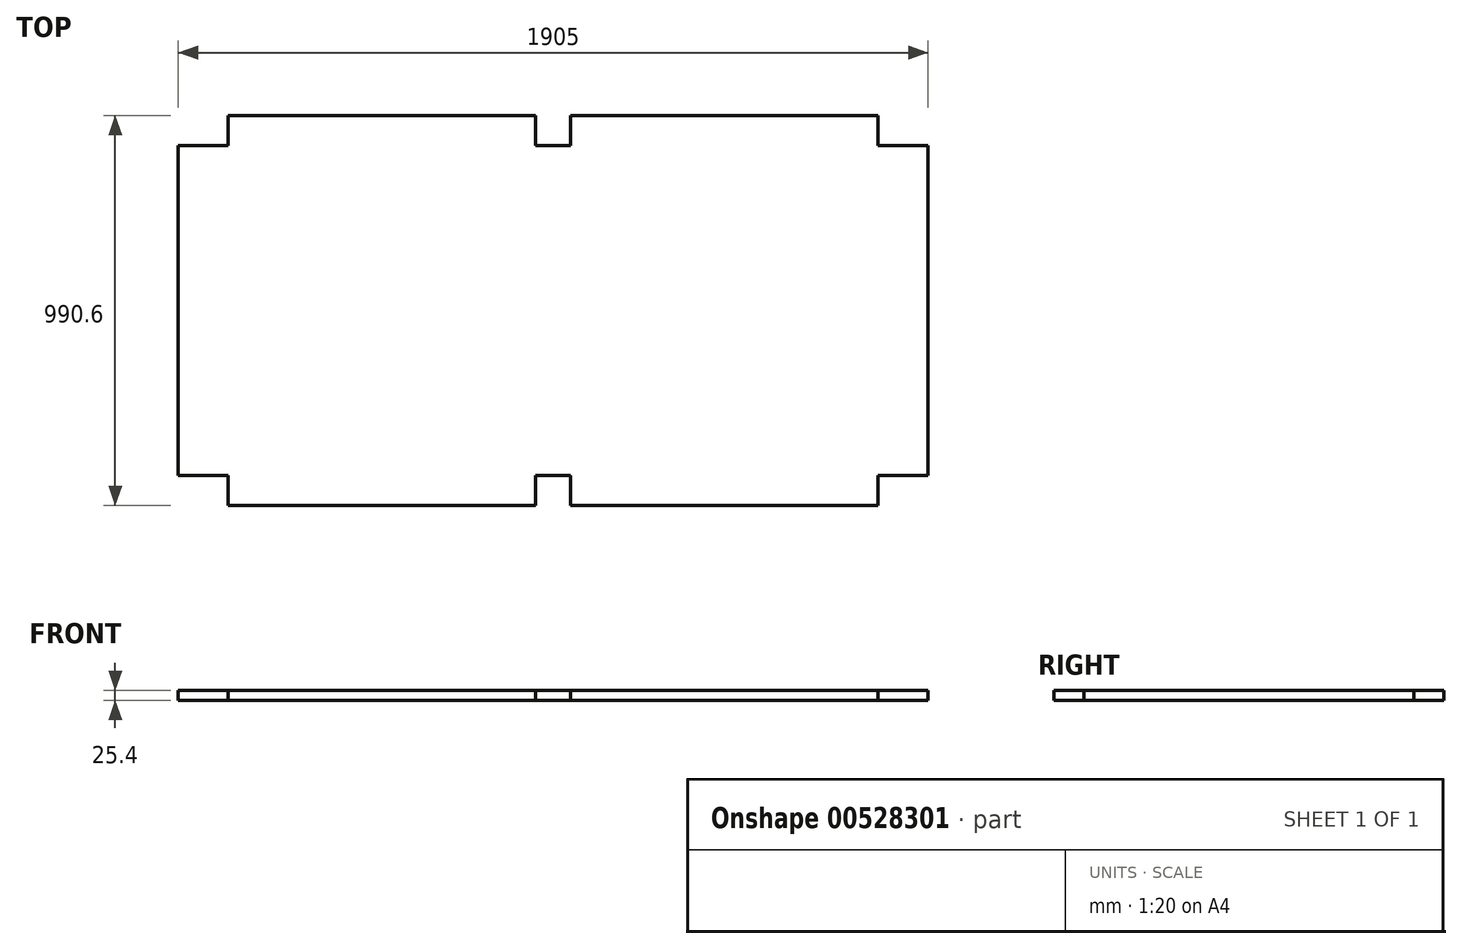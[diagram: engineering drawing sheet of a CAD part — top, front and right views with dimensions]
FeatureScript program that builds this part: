
annotation { "Feature Type Name" : "Feature", "Feature Type Description" : "" }
export const myFeature = defineFeature(function(context is Context, id is Id, definition is map)
    precondition{}
    {
        {
            var Q0;
            Q0=qCreatedBy(makeId("Top.planeOp"),FACE);
            var sketch = newSketch(context, id + "F0", { "sketchPlane" : qUnion([Q0])});
            skLineSegment(sketch, "E0.bottom", {"start": v(952.5, -495.3) * mm, "end": v(-952.5, -495.3) * mm});
            skLineSegment(sketch, "E0.top", {"start": v(952.5, 495.3) * mm, "end": v(-952.5, 495.3) * mm});
            skLineSegment(sketch, "E0.left", {"start": v(952.5, -495.3) * mm, "end": v(952.5, 495.3) * mm});
            skLineSegment(sketch, "E0.right", {"start": v(-952.5, -495.3) * mm, "end": v(-952.5, 495.3) * mm});
            skPoint(sketch, "E0.middle", {"position": v(0, 0) * mm});
            skLineSegment(sketch, "E1", {"start": v(-952.5, -419.1) * mm, "end": v(-825.5, -419.1) * mm});
            skLineSegment(sketch, "E2", {"start": v(-825.5, -419.1) * mm, "end": v(-825.5, -495.3) * mm});
            skLineSegment(sketch, "E3", {"start": v(825.5, -495.3) * mm, "end": v(825.5, -419.1) * mm});
            skLineSegment(sketch, "E4", {"start": v(825.5, -419.1) * mm, "end": v(952.5, -419.1) * mm});
            skLineSegment(sketch, "E5", {"start": v(825.5, 495.3) * mm, "end": v(825.5, 419.1) * mm});
            skLineSegment(sketch, "E6", {"start": v(825.5, 419.1) * mm, "end": v(952.5, 419.1) * mm});
            skLineSegment(sketch, "E7", {"start": v(-952.5, 419.1) * mm, "end": v(-825.5, 419.1) * mm});
            skLineSegment(sketch, "E8", {"start": v(-825.5, 419.1) * mm, "end": v(-825.5, 495.3) * mm});
            skLineSegment(sketch, "E9", {"start": v(-44.45, 495.3) * mm, "end": v(-44.45, 419.1) * mm});
            skLineSegment(sketch, "E10", {"start": v(-44.45, 419.1) * mm, "end": v(44.45, 419.1) * mm});
            skLineSegment(sketch, "E11", {"start": v(44.45, 419.1) * mm, "end": v(44.45, 495.3) * mm});
            skLineSegment(sketch, "E12", {"start": v(-44.45, -495.3) * mm, "end": v(-44.45, -419.1) * mm});
            skLineSegment(sketch, "E13", {"start": v(-44.45, -419.1) * mm, "end": v(44.45, -419.1) * mm});
            skLineSegment(sketch, "E14", {"start": v(44.45, -419.1) * mm, "end": v(44.45, -495.3) * mm});
            skSolve(sketch);
        }
        {
            var Q0;
            {var subQ1=sQuery(id+"F0.wireOp",EDGE,"E1");Q0=makeQuery(id+"F0.imprint","IMPRINT",FACE,{"disambiguationData":[TD([[makeQuery(id+"F0.imprint","IMPRINT",EDGE,{"derivedFrom":subQ1}),1.0]])]});}
            extrude(context, id + "F1", {"entities" : qUnion([Q0]), "depth" : 25.4 * mm, "offsetDistance" : 25.4 * mm});
        }
    });
